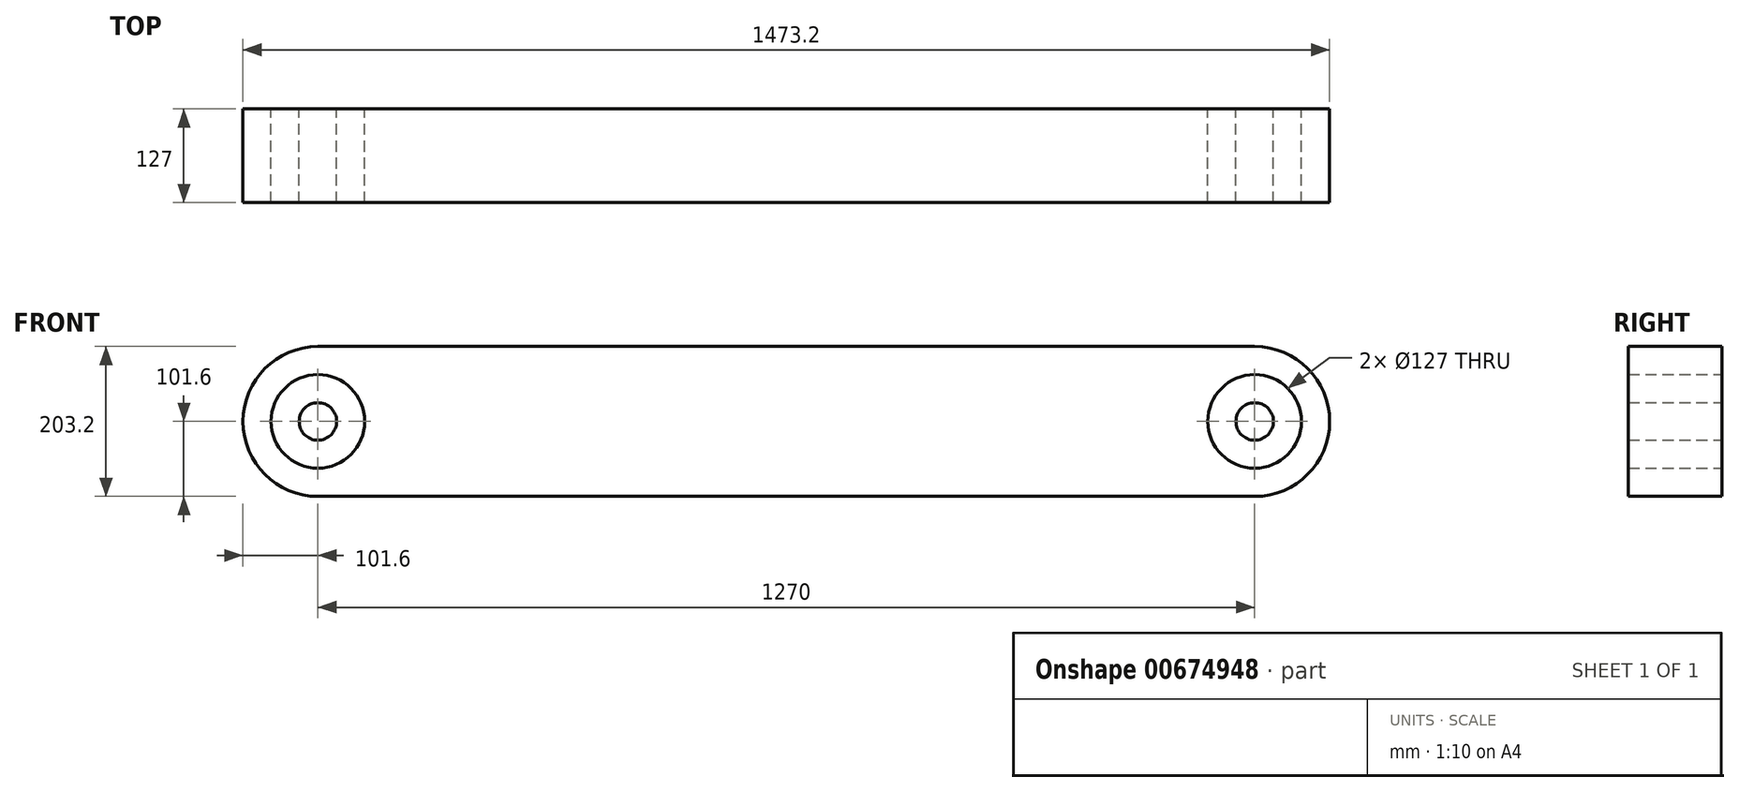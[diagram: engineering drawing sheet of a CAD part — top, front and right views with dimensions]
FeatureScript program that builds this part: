
annotation { "Feature Type Name" : "Feature", "Feature Type Description" : "" }
export const myFeature = defineFeature(function(context is Context, id is Id, definition is map)
    precondition{}
    {
        {
            var Q0;
            Q0=qCreatedBy(makeId("Front.planeOp"),FACE);
            var sketch = newSketch(context, id + "F0", { "sketchPlane" : qUnion([Q0])});
            skLineSegment(sketch, "E0.bottom", {"start": v(0, 0) * mm, "end": v(1270, 0) * mm});
            skLineSegment(sketch, "E0.top", {"start": v(0, 203.2) * mm, "end": v(1270, 203.2) * mm});
            skArc(sketch, "E1", {"start": v(0, 203.2) * mm, "mid": v(-101.6, 101.6) * mm, "end": v(0, 0) * mm});
            skArc(sketch, "E2", {"start": v(1270, 0) * mm, "mid": v(1371.6, 101.6) * mm, "end": v(1270, 203.2) * mm});
            skCircle(sketch, "E3", {"center": v(0, 101.6) * mm, "radius": 63.5 * mm});
            skCircle(sketch, "E4", {"center": v(1270, 101.6) * mm, "radius": 63.5 * mm});
            skCircle(sketch, "E5", {"center": v(1270, 101.6) * mm, "radius": 25.4 * mm});
            skCircle(sketch, "E6", {"center": v(0, 101.6) * mm, "radius": 25.4 * mm});
            skSolve(sketch);
        }
        {
            var Q0;
            Q0=makeQuery(id+"F0.imprint","IMPRINT",FACE,{"disambiguationData":[TD([[makeQuery(id+"F0.imprint","IMPRINT",EDGE,{"derivedFrom":sQuery(id+"F0.wireOp",EDGE,"E0.bottom")}),1.0]])]});
            var Q1;
            Q1=makeQuery(id+"F0.imprint","IMPRINT",FACE,{"disambiguationData":[TD([[makeQuery(id+"F0.imprint","IMPRINT",EDGE,{"derivedFrom":sQuery(id+"F0.wireOp",EDGE,"E6")}),1.0]])]});
            var Q2;
            Q2=makeQuery(id+"F0.imprint","IMPRINT",FACE,{"disambiguationData":[TD([[makeQuery(id+"F0.imprint","IMPRINT",EDGE,{"derivedFrom":sQuery(id+"F0.wireOp",EDGE,"E5")}),1.0]])]});
            extrude(context, id + "F1", {"entities" : qUnion([Q0, Q1, Q2]), "depth" : 127 * mm, "offsetDistance" : 25.4 * mm});
        }
    });
